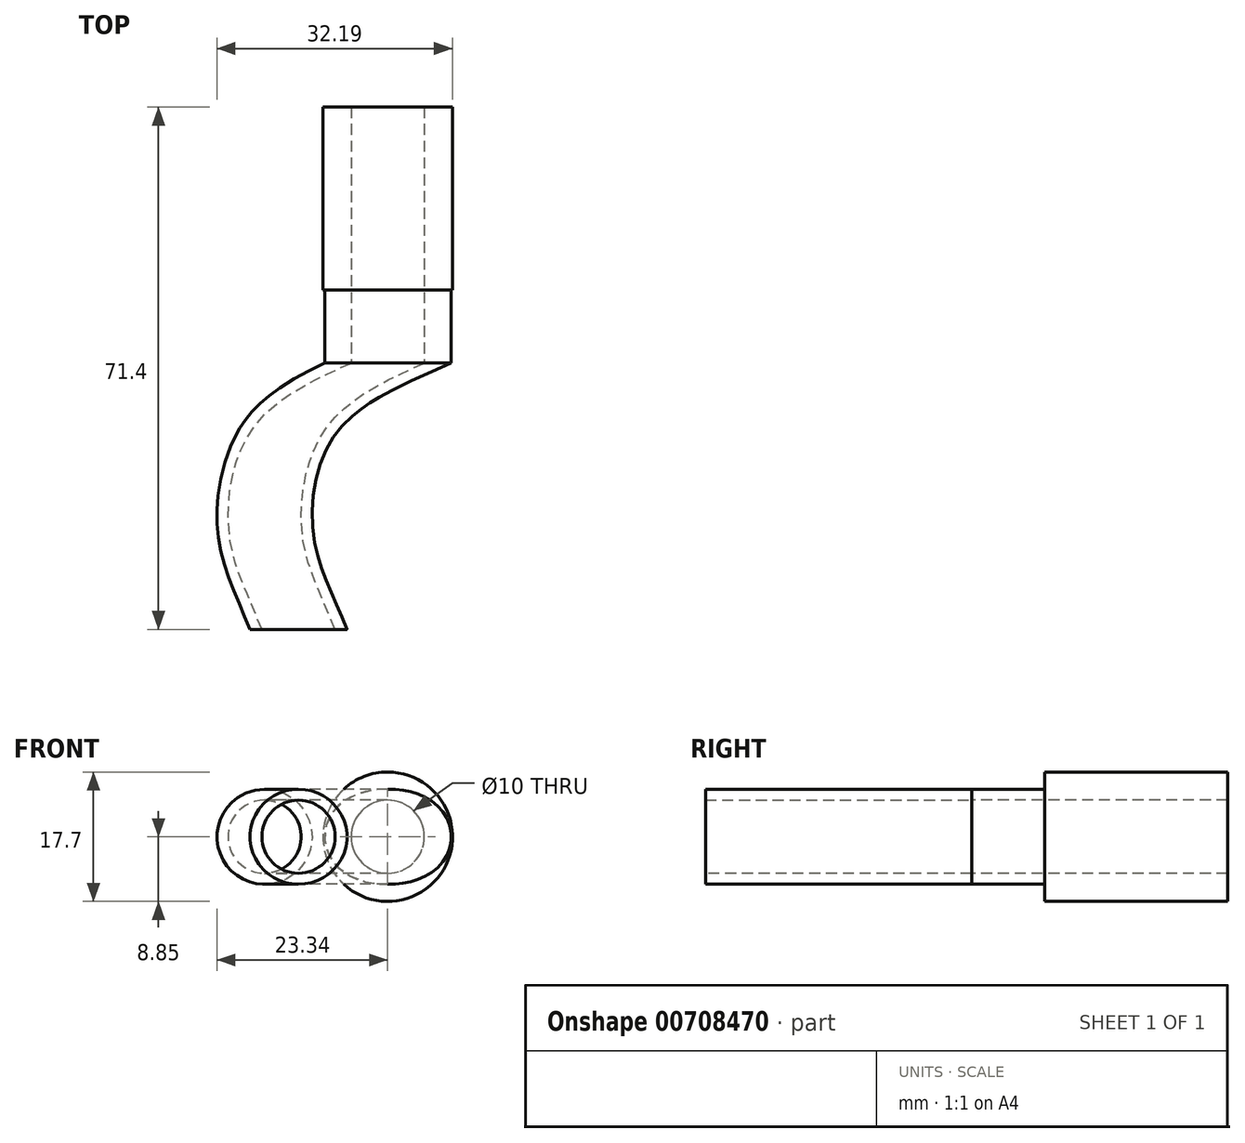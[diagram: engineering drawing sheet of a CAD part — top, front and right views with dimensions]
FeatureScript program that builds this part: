
annotation { "Feature Type Name" : "Feature", "Feature Type Description" : "" }
export const myFeature = defineFeature(function(context is Context, id is Id, definition is map)
    precondition{}
    {
        {
            var Q0;
            Q0=qCreatedBy(makeId("Front.planeOp"),FACE);
            var sketch = newSketch(context, id + "F0", { "sketchPlane" : qUnion([Q0])});
            skCircle(sketch, "E0", {"center": v(0, 0) * mm, "radius": 5 * mm});
            skSolve(sketch);
        }
        {
            var Q0;
            Q0=qCreatedBy(makeId("Top.planeOp"),FACE);
            var sketch = newSketch(context, id + "F1", { "sketchPlane" : qUnion([Q0])});
            skFitSpline(sketch, "E1", {"points": [v(0, 0) * mm, v(0, -32.44) * mm], "startDerivative": vector(0, -46.16) * mm, "endDerivative": vector(0, -46.16) * mm});
            skFitSpline(sketch, "E2", {"points": [v(0, 0) * mm, v(7.45, -3.7) * mm, v(13.39, -8.84) * mm, v(16.29, -15.7) * mm, v(16.81, -21.9) * mm, v(16.02, -26.77) * mm, v(14.3, -31.39) * mm, v(12.2, -36.4) * mm], "startDerivative": vector(46.82, -20.85) * mm, "endDerivative": vector(-16.24, -38.4) * mm});
            skFitSpline(sketch, "E3.MirrorCS", {"points": [v(0, 0) * mm, v(-7.45, -3.7) * mm, v(-13.39, -8.84) * mm, v(-16.29, -15.7) * mm, v(-16.81, -21.9) * mm, v(-16.02, -26.77) * mm, v(-14.3, -31.39) * mm, v(-12.2, -36.4) * mm], "startDerivative": vector(-46.82, -20.85) * mm, "endDerivative": vector(16.24, -38.4) * mm});
            skSolve(sketch);
        }
        {
            var Q0;
            Q0=makeQuery(id+"F0.imprint","IMPRINT",FACE,{"disambiguationData":[TD([[makeQuery(id+"F0.imprint","IMPRINT",EDGE,{"derivedFrom":sQuery(id+"F0.wireOp",EDGE,"E0")}),1.0]])]});
            var Q1;
            Q1=sQuery(id+"F1.wireOp",EDGE,"E3.MirrorCS");
            sweep(context, id + "F2", {"profiles" : qUnion([Q0]), "path" : qUnion([Q1]), "keepProfileOrientation" : true});
        }
        {
            var Q0;
            Q0=makeQuery(id+"F0.imprint","IMPRINT",FACE,{"disambiguationData":[TD([[makeQuery(id+"F0.imprint","IMPRINT",EDGE,{"derivedFrom":sQuery(id+"F0.wireOp",EDGE,"E0")}),1.0]])]});
            var Q1;
            Q1=sQuery(id+"F1.wireOp",EDGE,"E2");
            sweep(context, id + "F3", {"operationType" : NewBodyOperationType.ADD, "profiles" : qUnion([Q0]), "path" : qUnion([Q1]), "keepProfileOrientation" : true});
        }
        {
            var Q0;
            Q0=makeQuery(id+"F2.opSweep","CAP_FACE",FACE,{"disambiguationData":[OSD([sQuery(id+"F0.wireOp",EDGE,"E0"),sQuery(id+"F1.wireOp",VERTEX,"E3.MirrorCS.end")])],"isStart":false});
            var Q1;
            Q1=makeQuery(id+"F3.opSweep","CAP_FACE",FACE,{"disambiguationData":[OSD([sQuery(id+"F0.wireOp",EDGE,"E0"),sQuery(id+"F1.wireOp",VERTEX,"E2.end")])],"isStart":false});
            var Q2;
            Q2=makeQuery(id+"F2.opSweep","CAP_FACE",FACE,{"disambiguationData":[OSD([sQuery(id+"F0.wireOp",EDGE,"E0"),sQuery(id+"F1.wireOp",VERTEX,"E3.MirrorCS.start")])],"isStart":true});
            shell(context, id + "F4", {"entities" : qUnion([Q0, Q1, Q2]), "thickness" : 1.5 * mm, "oppositeDirection" : true});
        }
        {
            var Q0;
            Q0=makeQuery(id+"F2.opSweep","CAP_FACE",FACE,{"disambiguationData":[OSD([sQuery(id+"F0.wireOp",EDGE,"E0"),sQuery(id+"F1.wireOp",VERTEX,"E3.MirrorCS.start")])],"isStart":true});
            extrude(context, id + "F5", {"entities" : qUnion([Q0]), "operationType" : NewBodyOperationType.ADD, "depth" : 10 * mm, "offsetDistance" : 25 * mm});
        }
        {
            var Q0;
            Q0=qCreatedBy(makeId("Front.planeOp"),FACE);
            cPlane(context, id + "F6", {"entities" : qUnion([Q0]), "cplaneType" : CPlaneType.OFFSET, "offset" : 35 * mm, "oppositeDirection" : true, "width" : 150 * mm, "height" : 150 * mm});
        }
        {
            var Q0;
            Q0=makeQuery(id+"F5.opExtrude","CAP_FACE",FACE,{"disambiguationData":[OSD([sQuery(id+"F0.wireOp",EDGE,"E0"),sQuery(id+"F1.wireOp",VERTEX,"E3.MirrorCS.start")])],"isStart":false});
            var sketch = newSketch(context, id + "F7", { "sketchPlane" : qUnion([Q0])});
            skCircle(sketch, "E4", {"center": v(0, 0) * mm, "radius": 8.85 * mm});
            skSolve(sketch);
        }
        {
            var Q0;
            {var subQ0=sQuery(id+"F7.wireOp",EDGE,"E4");var subQ2=sQuery(id+"F0.wireOp",EDGE,"E0");var subQ3=sQuery(id+"F1.wireOp",VERTEX,"E3.MirrorCS.start");var subQ6=makeQuery(id+"F5.opExtrude","CAP_EDGE",EDGE,{"disambiguationData":[OSD([subQ2,subQ3])],"isStart":false});var subQ7=makeQuery(id+"F7.imprint","INTERSECT",VERTEX,{"disambiguationData":[OD(1.0)],"derivedFrom":[subQ6,subQ0]});Q0=makeQuery(id+"F7.imprint","IMPRINT",FACE,{"disambiguationData":[TD([[makeQuery(id+"F7.imprint","IMPRINT",EDGE,{"disambiguationData":[TD([[subQ7,1.0]])],"derivedFrom":subQ0}),1.0]])]});}
            var Q1;
            {var subQ0=sQuery(id+"F7.wireOp",EDGE,"E4");var subQ2=sQuery(id+"F0.wireOp",EDGE,"E0");var subQ3=sQuery(id+"F1.wireOp",VERTEX,"E3.MirrorCS.start");var subQ6=makeQuery(id+"F5.opExtrude","CAP_EDGE",EDGE,{"disambiguationData":[OSD([subQ2,subQ3])],"isStart":false});var subQ7=makeQuery(id+"F7.imprint","INTERSECT",VERTEX,{"disambiguationData":[OD(0.0)],"derivedFrom":[subQ6,subQ0]});Q1=makeQuery(id+"F7.imprint","IMPRINT",FACE,{"disambiguationData":[TD([[makeQuery(id+"F7.imprint","IMPRINT",EDGE,{"disambiguationData":[TD([[subQ7,-1.0]])],"derivedFrom":subQ0}),1.0]])]});}
            var Q2;
            {var subQ0=sQuery(id+"F1.wireOp",VERTEX,"E3.MirrorCS.start");var subQ1=sQuery(id+"F0.wireOp",EDGE,"E0");var subQ3=sQuery(id+"F1.wireOp",VERTEX,"E2.start");Q2=makeQuery(id+"F7.imprint","IMPRINT",FACE,{"disambiguationData":[TD([[makeQuery(id+"F7.imprint","IMPRINT",EDGE,{"derivedFrom":makeQuery(id+"F5.opExtrude","CAP_EDGE",EDGE,{"disambiguationData":[OSD([subQ1,subQ3,subQ0]),TDD([makeQuery(id+"F4.opShell","OFFSET_EDGE",EDGE,{"disambiguationData":[OSD([subQ1,subQ3,subQ0])]}),makeQuery(id+"F4.opShell","OFFSET_EDGE",EDGE,{"disambiguationData":[OSD([subQ1,subQ0])]})])],"isStart":false})}),1.0]])]});}
            extrude(context, id + "F8", {"entities" : qUnion([Q0, Q1, Q2]), "operationType" : NewBodyOperationType.ADD, "depth" : 25 * mm, "offsetDistance" : 25 * mm});
        }
    });
